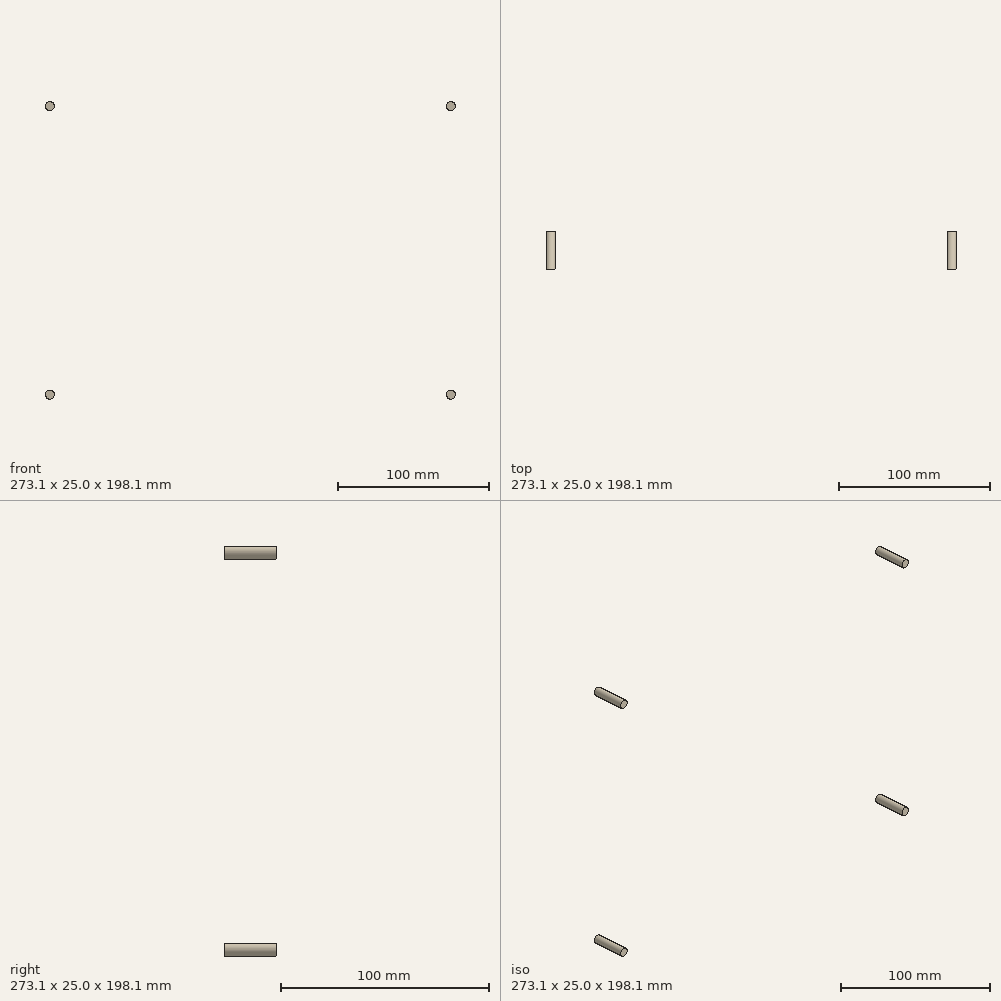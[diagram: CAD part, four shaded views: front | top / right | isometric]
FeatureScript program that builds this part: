
annotation { "Feature Type Name" : "Feature", "Feature Type Description" : "" }
export const myFeature = defineFeature(function(context is Context, id is Id, definition is map)
    precondition{}
    {
        {
            var Q0;
            Q0=qCreatedBy(makeId("Front.planeOp"),FACE);
            var sketch = newSketch(context, id + "F0", { "sketchPlane" : qUnion([Q0])});
            skLineSegment(sketch, "E0", {"start": v(-133.5, 152.6) * mm, "end": v(-133.5, -156.11) * mm, "construction": true});
            skLineSegment(sketch, "E1", {"start": v(-182.25, 96) * mm, "end": v(222.32, 96) * mm, "construction": true});
            skLineSegment(sketch, "E2", {"start": v(133.5, 154.72) * mm, "end": v(133.5, -148.17) * mm, "construction": true});
            skLineSegment(sketch, "E3", {"start": v(223.38, -96) * mm, "end": v(-237.85, -96) * mm, "construction": true});
            skCircle(sketch, "E4", {"center": v(-133.5, 96) * mm, "radius": 3.02 * mm});
            skCircle(sketch, "E5", {"center": v(-133.5, -96) * mm, "radius": 3.02 * mm});
            skCircle(sketch, "E6", {"center": v(133.5, -96) * mm, "radius": 3.02 * mm});
            skCircle(sketch, "E7", {"center": v(133.5, 96) * mm, "radius": 3.02 * mm});
            skSolve(sketch);
        }
        {
            var Q0;
            Q0 = qSketchRegion(id + "F0", true);
            extrude(context, id + "F1", {"entities" : qUnion([Q0]), "depth" : 25 * mm, "offsetDistance" : 25 * mm});
        }
    });
